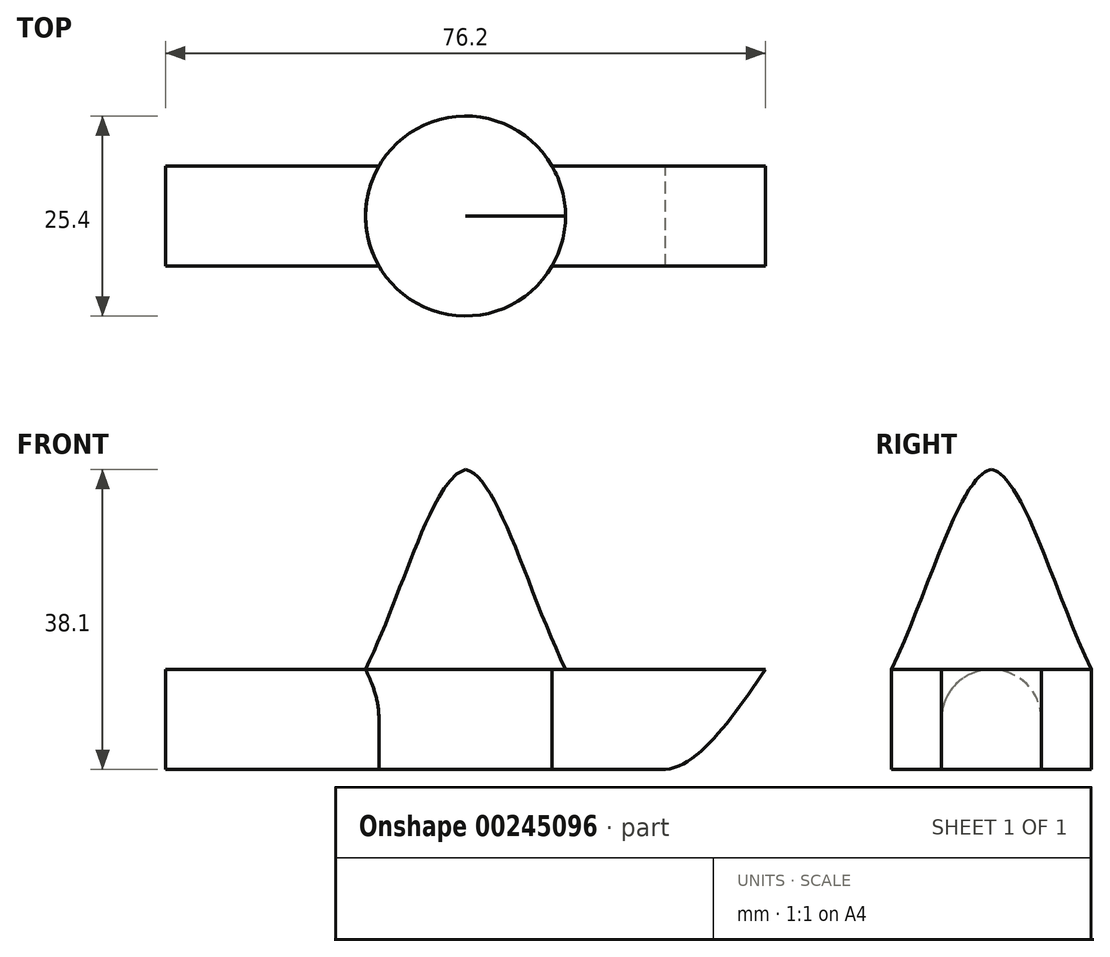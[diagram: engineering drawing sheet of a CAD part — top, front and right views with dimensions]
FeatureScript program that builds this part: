
annotation { "Feature Type Name" : "Feature", "Feature Type Description" : "" }
export const myFeature = defineFeature(function(context is Context, id is Id, definition is map)
    precondition{}
    {
        {
            var Q0;
            Q0=qCreatedBy(makeId("Front.planeOp"),FACE);
            var sketch = newSketch(context, id + "F0", { "sketchPlane" : qUnion([Q0])});
            skLineSegment(sketch, "E0", {"start": v(0, 0) * mm, "end": v(0, 25.4) * mm});
            skLineSegment(sketch, "E1", {"start": v(0, 0) * mm, "end": v(12.7, 0) * mm});
            skLineSegment(sketch, "E2", {"start": v(12.7, 0) * mm, "end": v(12.7, -12.7) * mm});
            skLineSegment(sketch, "E3", {"start": v(12.7, -12.7) * mm, "end": v(25.4, -12.7) * mm});
            skLineSegment(sketch, "E4.MirrorCS", {"start": v(0, 0) * mm, "end": v(-12.7, 0) * mm});
            skLineSegment(sketch, "E5.top", {"start": v(0, -12.7) * mm, "end": v(12.7, -12.7) * mm});
            skLineSegment(sketch, "E5.left", {"start": v(0, 0) * mm, "end": v(0, -12.7) * mm});
            skLineSegment(sketch, "E6", {"start": v(25.4, -12.7) * mm, "end": v(25.4, -12.7) * mm});
            skLineSegment(sketch, "E7.bottom", {"start": v(0, -12.7) * mm, "end": v(25.4, -12.7) * mm});
            skLineSegment(sketch, "E7.top", {"start": v(0, -15.88) * mm, "end": v(25.4, -15.88) * mm});
            skLineSegment(sketch, "E7.left", {"start": v(0, -12.7) * mm, "end": v(0, -15.88) * mm});
            skLineSegment(sketch, "E7.right", {"start": v(25.4, -12.7) * mm, "end": v(25.4, -15.88) * mm});
            skLineSegment(sketch, "E8", {"start": v(25.4, -12.7) * mm, "end": v(38.1, -12.7) * mm});
            skLineSegment(sketch, "E9", {"start": v(38.1, -12.7) * mm, "end": v(38.1, 0) * mm});
            skFitSpline(sketch, "E10", {"points": [v(-12.7, 0) * mm, v(0, 25.4) * mm, v(12.7, 0) * mm, v(25.4, -12.7) * mm, v(38.1, 0) * mm], "startDerivative": vector(46.53, 140.84) * mm, "endDerivative": vector(56.6, 82.8) * mm});
            skLineSegment(sketch, "E11.bottom", {"start": v(0, 0) * mm, "end": v(38.1, 0) * mm});
            skLineSegment(sketch, "E11.top", {"start": v(0, -12.7) * mm, "end": v(38.1, -12.7) * mm});
            skLineSegment(sketch, "E11.right", {"start": v(38.1, 0) * mm, "end": v(38.1, -12.7) * mm});
            skLineSegment(sketch, "E12.bottom", {"start": v(0, 0) * mm, "end": v(-38.1, 0) * mm});
            skLineSegment(sketch, "E12.top", {"start": v(0, -12.7) * mm, "end": v(-38.1, -12.7) * mm});
            skLineSegment(sketch, "E12.right", {"start": v(-38.1, 0) * mm, "end": v(-38.1, -12.7) * mm});
            skSolve(sketch);
        }
        {
            var Q0;
            {var subQ0=sQuery(id+"F0.wireOp",EDGE,"E0");Q0=makeQuery(id+"F0.imprint","IMPRINT",FACE,{"disambiguationData":[TD([[makeQuery(id+"F0.imprint","IMPRINT",EDGE,{"derivedFrom":subQ0}),-1.0]])]});}
            var Q1;
            Q1=makeQuery(id+"F0.imprint","IMPRINT",FACE,{"disambiguationData":[TD([[makeQuery(id+"F0.imprint","IMPRINT",EDGE,{"derivedFrom":sQuery(id+"F0.wireOp",EDGE,"E1")}),-1.0]])]});
            var Q2;
            {var subQ0=sQuery(id+"F0.wireOp",EDGE,"E2");Q2=makeQuery(id+"F0.imprint","IMPRINT",FACE,{"disambiguationData":[TD([[makeQuery(id+"F0.imprint","IMPRINT",EDGE,{"derivedFrom":subQ0}),-1.0]])]});}
            var Q3;
            Q3=sQuery(id+"F0.wireOp",EDGE,"E5.left");
            revolve(context, id + "F1", {"entities" : qUnion([Q0, Q1, Q2]), "axis" : qUnion([Q3]), "revolveType" : RevolveType.FULL});
        }
        {
            var Q0;
            Q0=makeQuery(id+"F0.imprint","IMPRINT",FACE,{"disambiguationData":[TD([[makeQuery(id+"F0.imprint","IMPRINT",EDGE,{"derivedFrom":sQuery(id+"F0.wireOp",EDGE,"E12.top")}),-1.0]])]});
            var Q1;
            {var subQ0=sQuery(id+"F0.wireOp",EDGE,"E2");Q1=makeQuery(id+"F0.imprint","IMPRINT",FACE,{"disambiguationData":[TD([[makeQuery(id+"F0.imprint","IMPRINT",EDGE,{"derivedFrom":subQ0}),1.0]])]});}
            var Q2;
            {var subQ1=sQuery(id+"F0.wireOp",EDGE,"E10");var subQ3=sQuery(id+"F0.wireOp",EDGE,"E11.top");var subQ4=makeQuery(id+"F0.imprint","INTERSECT",VERTEX,{"derivedFrom":[subQ1,subQ3]});Q2=makeQuery(id+"F0.imprint","IMPRINT",FACE,{"disambiguationData":[TD([[makeQuery(id+"F0.imprint","IMPRINT",EDGE,{"disambiguationData":[TD([[subQ4,1.0]])],"derivedFrom":subQ1}),1.0]])]});}
            var Q3;
            {var subQ3=sQuery(id+"F0.wireOp",EDGE,"E11.right");Q3=makeQuery(id+"F0.imprint","IMPRINT",FACE,{"disambiguationData":[TD([[makeQuery(id+"F0.imprint","IMPRINT",EDGE,{"derivedFrom":subQ3}),-1.0]])]});}
            var Q4;
            {var subQ0=sQuery(id+"F0.wireOp",EDGE,"E2");Q4=makeQuery(id+"F0.imprint","IMPRINT",FACE,{"disambiguationData":[TD([[makeQuery(id+"F0.imprint","IMPRINT",EDGE,{"derivedFrom":subQ0}),-1.0]])]});}
            extrude(context, id + "F2", {"entities" : qUnion([Q0, Q1, Q2, Q3, Q4]), "operationType" : NewBodyOperationType.ADD, "endBound" : BoundingType.SYMMETRIC, "depth" : 12.7 * mm});
        }
        {
            var Q0;
            {var subQ0=sQuery(id+"F0.wireOp",EDGE,"E12.bottom");var subQ1=sQuery(id+"F0.wireOp",EDGE,"E11.bottom");var subQ2=sQuery(id+"F0.wireOp",EDGE,"E12.right");Q0=makeQuery(id+"F2.boolean.opBoolean","SPLIT",EDGE,{"disambiguationData":[TD([makeQuery(id+"F2.opExtrude","SWEPT_FACE",FACE,{"disambiguationData":[OSD([subQ2])]})])],"derivedFrom":makeQuery(id+"F2.opExtrude","CAP_EDGE",EDGE,{"disambiguationData":[OSD([subQ1,subQ0])],"isStart":false})});}
            var Q1;
            {var subQ0=sQuery(id+"F0.wireOp",EDGE,"E12.bottom");var subQ1=sQuery(id+"F0.wireOp",EDGE,"E11.bottom");var subQ2=sQuery(id+"F0.wireOp",EDGE,"E11.right");Q1=makeQuery(id+"F2.boolean.opBoolean","SPLIT",EDGE,{"disambiguationData":[TD([makeQuery(id+"F2.opExtrude","SWEPT_FACE",FACE,{"disambiguationData":[OSD([subQ2])]})])],"derivedFrom":makeQuery(id+"F2.opExtrude","CAP_EDGE",EDGE,{"disambiguationData":[OSD([subQ1,subQ0])],"isStart":false})});}
            var Q2;
            {var subQ0=sQuery(id+"F0.wireOp",EDGE,"E12.bottom");var subQ1=sQuery(id+"F0.wireOp",EDGE,"E11.bottom");var subQ2=sQuery(id+"F0.wireOp",EDGE,"E11.right");Q2=makeQuery(id+"F2.boolean.opBoolean","SPLIT",EDGE,{"disambiguationData":[TD([makeQuery(id+"F2.opExtrude","SWEPT_FACE",FACE,{"disambiguationData":[OSD([subQ2])]})])],"derivedFrom":makeQuery(id+"F2.opExtrude","CAP_EDGE",EDGE,{"disambiguationData":[OSD([subQ1,subQ0])],"isStart":true})});}
            var Q3;
            {var subQ0=sQuery(id+"F0.wireOp",EDGE,"E12.bottom");var subQ1=sQuery(id+"F0.wireOp",EDGE,"E11.bottom");var subQ2=sQuery(id+"F0.wireOp",EDGE,"E12.right");Q3=makeQuery(id+"F2.boolean.opBoolean","SPLIT",EDGE,{"disambiguationData":[TD([makeQuery(id+"F2.opExtrude","SWEPT_FACE",FACE,{"disambiguationData":[OSD([subQ2])]})])],"derivedFrom":makeQuery(id+"F2.opExtrude","CAP_EDGE",EDGE,{"disambiguationData":[OSD([subQ1,subQ0])],"isStart":true})});}
            fillet(context, id + "F3", {"entities" : qUnion([Q0, Q1, Q2, Q3]), "radius" : 6.35 * mm, "tangentPropagation" : true, "allowEdgeOverflow" : false});
        }
    });
